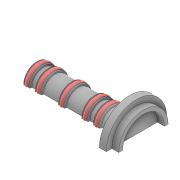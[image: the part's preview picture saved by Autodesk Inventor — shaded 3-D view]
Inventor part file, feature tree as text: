
AUTODESK INVENTOR PART (.ipt)
format: ipt  version: 2021 (Build 250183000, 183)  size: 555,520 bytes
history: native  units: in
note: dims shown in document units (in); Inventor stores cm internally (conversion verified against a paired STEP export)
features: revolve x3, sketch x3, chamfer x2, split x2, projected_geometry x1
ambient origin geometry x8: Origin, YZ Plane, XZ Plane, XY Plane, X Axis, Y Axis, Z Axis, Center Point
bodies: Solid1 (feature_tree), Solid5 (feature_tree)
feature tree (11):
  revolve  "Revolution1"  [1 undecoded]
  chamfer  "Chamfer1"  Distance=0.1378in
  chamfer  "Chamfer2"  Distance=0.0394in
  revolve  "Revolution6"  [1 undecoded]
  revolve  "Revolution7"  Angle=90.0deg
  split  "Split1"
  split  "Split2"
  sketch  "Sketch1"  dims[d2=0.0591in d3=0.0591in]
  sketch  "Sketch4"  dims[d4=0.0591in]
  sketch  "Sketch5"  dims[d5=0.0591in d9=0.1378in d10=0.0394in d14=0.2559in d15=90.0deg d53=0.0059in d54=0.0787in d55=45.0deg d57=0.0059in d58=0.0787in d59=45.0deg d60=0.2087in d61=0.1772in d62=0.0591in d63=0.0984in d64=0.0394in d65=0.1575in d95=0.0591in d96=0.1378in d107=0.0394in d108=0.0591in d124=0.0118in d125=0.0118in d126=0.0217in d127=0.0118in d128=0.0118in d129=0.0217in d130=0.0118in d131=0.0118in d133=0.0217in d134=0.0118in d135=0.0118in d136=0.0217in d137=0.0118in d138=0.0118in d139=0.0217in d140=90.0deg d141=0.0079in d142=0.037in d143=0.0059in d144=0.0059in d145=0.0079in d146=0.7874in d148=0.0984in d149=0.3937in d151=0.3937in d153=0.7874in d155=0.4921in d156=0.3937in d158=0.3937in d160=0.7874in d162=0.2953in d163=0.3937in d165=0.3937in d167=90.0deg]
  projected_geometry  "Project Cut Edges4"
note: 2 required parameter values undecoded (feature->parameter linkage not recoverable at this tier; creation-order binding heuristic only, values carry confidence <= 0.55)
